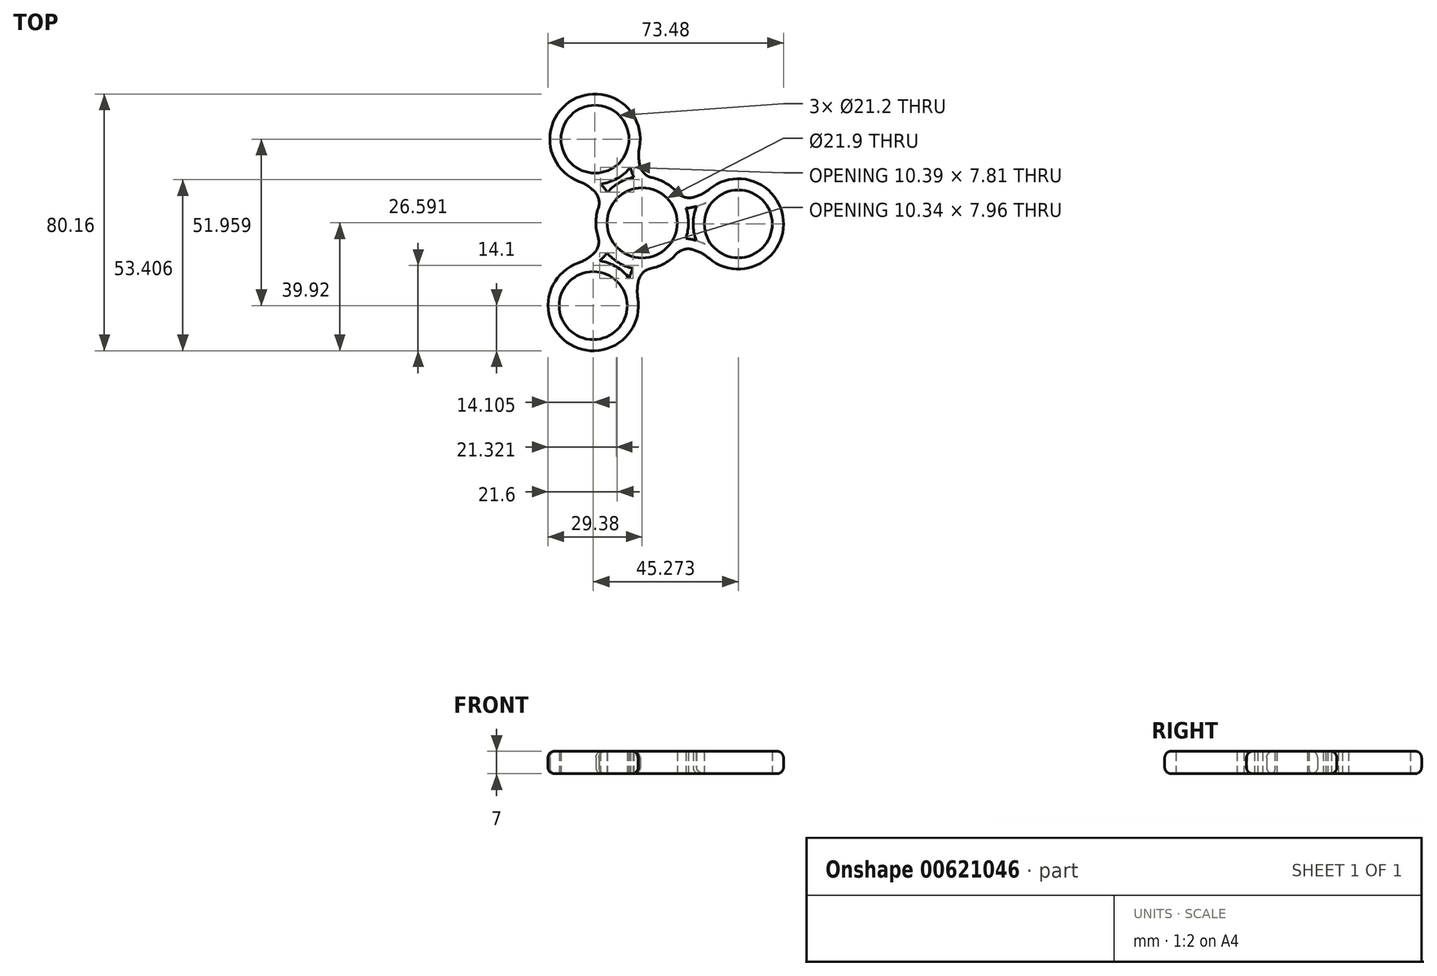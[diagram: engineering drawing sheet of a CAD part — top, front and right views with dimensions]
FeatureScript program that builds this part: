
annotation { "Feature Type Name" : "Feature", "Feature Type Description" : "" }
export const myFeature = defineFeature(function(context is Context, id is Id, definition is map)
    precondition{}
    {
        {
            var Q0;
            Q0=qCreatedBy(makeId("Top.planeOp"),FACE);
            var sketch = newSketch(context, id + "F0", { "sketchPlane" : qUnion([Q0])});
            skCircle(sketch, "E0", {"center": v(0, 0) * mm, "radius": 10.95 * mm});
            skCircle(sketch, "E1.0", {"center": v(0, 0) * mm, "radius": 14.45 * mm});
            skCircle(sketch, "E2.cCircle", {"center": v(0, 0) * mm, "radius": 15 * mm, "construction": true});
            skLineSegment(sketch, "E2.0", {"start": v(-14.72, 26.14) * mm, "end": v(30, -0.32) * mm, "construction": true});
            skLineSegment(sketch, "E2.1", {"start": v(30, -0.32) * mm, "end": v(-15.28, -25.82) * mm, "construction": true});
            skLineSegment(sketch, "E2.2", {"start": v(-15.28, -25.82) * mm, "end": v(-14.72, 26.14) * mm, "construction": true});
            skPoint(sketch, "E2.0.midPoint", {"position": v(7.64, 12.9) * mm});
            skCircle(sketch, "E3", {"center": v(-14.72, 26.14) * mm, "radius": 10.6 * mm});
            skCircle(sketch, "E4", {"center": v(30, -0.32) * mm, "radius": 10.6 * mm});
            skCircle(sketch, "E5", {"center": v(-15.28, -25.82) * mm, "radius": 10.6 * mm});
            skCircle(sketch, "E6.0", {"center": v(-14.72, 26.14) * mm, "radius": 14.1 * mm});
            skCircle(sketch, "E7.0", {"center": v(-15.28, -25.82) * mm, "radius": 14.1 * mm});
            skCircle(sketch, "E8.0", {"center": v(30, -0.32) * mm, "radius": 14.1 * mm});
            skArc(sketch, "E9", {"start": v(-0.86, 23.57) * mm, "mid": v(5.58, 9.42) * mm, "end": v(21.07, 10.6) * mm});
            skArc(sketch, "E10", {"start": v(20.84, -11.04) * mm, "mid": v(5.37, -9.54) * mm, "end": v(-1.36, -23.55) * mm});
            skArc(sketch, "E11", {"start": v(-19.99, -12.53) * mm, "mid": v(-10.95, 0.12) * mm, "end": v(-19.71, 12.95) * mm});
            skArc(sketch, "E12.0", {"start": v(-18.98, -15.36) * mm, "mid": v(-7.95, 0.08) * mm, "end": v(-18.65, 15.76) * mm});
            skArc(sketch, "E13.0", {"start": v(-3.8, 24.12) * mm, "mid": v(4.05, 6.84) * mm, "end": v(22.97, 8.27) * mm});
            skArc(sketch, "E14.0", {"start": v(22.8, -8.76) * mm, "mid": v(3.9, -6.93) * mm, "end": v(-4.32, -24.03) * mm});
            skSolve(sketch);
        }
        {
            var Q0;
            Q0=qSketchRegion(id+"F0",true);
            var Q1;
            {var subQ0=sQuery(id+"F0.wireOp",EDGE,"E13.0");var subQ1=sQuery(id+"F0.wireOp",EDGE,"E0");var subQ2=makeQuery(id+"F0.imprint","INTERSECT",VERTEX,{"disambiguationData":[OD(1.0)],"derivedFrom":[subQ1,subQ0]});Q1=makeQuery(id+"F0.imprint","IMPRINT",FACE,{"disambiguationData":[TD([[makeQuery(id+"F0.imprint","IMPRINT",EDGE,{"disambiguationData":[TD([[subQ2,-1.0]])],"derivedFrom":subQ1}),-1.0]])]});}
            var Q2;
            {var subQ0=sQuery(id+"F0.wireOp",EDGE,"E13.0");var subQ1=sQuery(id+"F0.wireOp",EDGE,"E0");var subQ2=makeQuery(id+"F0.imprint","INTERSECT",VERTEX,{"disambiguationData":[OD(0.0)],"derivedFrom":[subQ1,subQ0]});Q2=makeQuery(id+"F0.imprint","IMPRINT",FACE,{"disambiguationData":[TD([[makeQuery(id+"F0.imprint","IMPRINT",EDGE,{"disambiguationData":[TD([[subQ2,1.0]])],"derivedFrom":subQ1}),-1.0]])]});}
            var Q3;
            {var subQ0=sQuery(id+"F0.wireOp",EDGE,"E12.0");var subQ1=sQuery(id+"F0.wireOp",EDGE,"E0");var subQ2=makeQuery(id+"F0.imprint","INTERSECT",VERTEX,{"disambiguationData":[OD(1.0)],"derivedFrom":[subQ1,subQ0]});Q3=makeQuery(id+"F0.imprint","IMPRINT",FACE,{"disambiguationData":[TD([[makeQuery(id+"F0.imprint","IMPRINT",EDGE,{"disambiguationData":[TD([[subQ2,-1.0]])],"derivedFrom":subQ1}),-1.0]])]});}
            extrude(context, id + "F1", {"entities" : qUnion([Q0, Q1, Q2, Q3]), "depth" : 7 * mm, "offsetDistance" : 25 * mm});
        }
        {
            var Q0;
            {var subQ0=sQuery(id+"F0.wireOp",EDGE,"E10");var subQ1=sQuery(id+"F0.wireOp",EDGE,"E1.0");Q0=makeQuery(id+"F1.opExtrude","SWEPT_EDGE",EDGE,{"disambiguationData":[OSD([subQ1,subQ0]),TDD([makeQuery(id+"F0.imprint","INTERSECT",VERTEX,{"disambiguationData":[OD(0.0)],"derivedFrom":[subQ1,subQ0]})])]});}
            var Q1;
            {var subQ0=sQuery(id+"F0.wireOp",EDGE,"E10");var subQ1=sQuery(id+"F0.wireOp",EDGE,"E1.0");Q1=makeQuery(id+"F1.opExtrude","SWEPT_EDGE",EDGE,{"disambiguationData":[OSD([subQ1,subQ0]),TDD([makeQuery(id+"F0.imprint","INTERSECT",VERTEX,{"disambiguationData":[OD(1.0)],"derivedFrom":[subQ1,subQ0]})])]});}
            var Q2;
            {var subQ0=sQuery(id+"F0.wireOp",EDGE,"E9");var subQ1=sQuery(id+"F0.wireOp",EDGE,"E1.0");Q2=makeQuery(id+"F1.opExtrude","SWEPT_EDGE",EDGE,{"disambiguationData":[OSD([subQ1,subQ0]),TDD([makeQuery(id+"F0.imprint","INTERSECT",VERTEX,{"disambiguationData":[OD(1.0)],"derivedFrom":[subQ1,subQ0]})])]});}
            var Q3;
            {var subQ0=sQuery(id+"F0.wireOp",EDGE,"E9");var subQ1=sQuery(id+"F0.wireOp",EDGE,"E1.0");Q3=makeQuery(id+"F1.opExtrude","SWEPT_EDGE",EDGE,{"disambiguationData":[OSD([subQ1,subQ0]),TDD([makeQuery(id+"F0.imprint","INTERSECT",VERTEX,{"disambiguationData":[OD(0.0)],"derivedFrom":[subQ1,subQ0]})])]});}
            var Q4;
            {var subQ0=sQuery(id+"F0.wireOp",EDGE,"E11");var subQ1=sQuery(id+"F0.wireOp",EDGE,"E1.0");Q4=makeQuery(id+"F1.opExtrude","SWEPT_EDGE",EDGE,{"disambiguationData":[OSD([subQ1,subQ0]),TDD([makeQuery(id+"F0.imprint","INTERSECT",VERTEX,{"disambiguationData":[OD(1.0)],"derivedFrom":[subQ1,subQ0]})])]});}
            var Q5;
            {var subQ0=sQuery(id+"F0.wireOp",EDGE,"E11");var subQ1=sQuery(id+"F0.wireOp",EDGE,"E1.0");Q5=makeQuery(id+"F1.opExtrude","SWEPT_EDGE",EDGE,{"disambiguationData":[OSD([subQ1,subQ0]),TDD([makeQuery(id+"F0.imprint","INTERSECT",VERTEX,{"disambiguationData":[OD(0.0)],"derivedFrom":[subQ1,subQ0]})])]});}
            fillet(context, id + "F2", {"entities" : qUnion([Q0, Q1, Q2, Q3, Q4, Q5]), "radius" : 5 * mm, "tangentPropagation" : true, "allowEdgeOverflow" : false});
        }
        {
            var Q0;
            Q0=makeQuery(id+"F1.opExtrude","CAP_EDGE",EDGE,{"disambiguationData":[OSD([sQuery(id+"F0.wireOp",EDGE,"E8.0")])],"isStart":true});
            var Q1;
            {var subQ0=sQuery(id+"F0.wireOp",EDGE,"E10");var subQ1=sQuery(id+"F0.wireOp",EDGE,"E1.0");Q1=makeQuery(id+"F1.opExtrude","CAP_EDGE",EDGE,{"disambiguationData":[OSD([subQ1]),TDD([makeQuery(id+"F0.imprint","IMPRINT",EDGE,{"disambiguationData":[TD([[makeQuery(id+"F0.imprint","INTERSECT",VERTEX,{"disambiguationData":[OD(0.0)],"derivedFrom":[subQ1,subQ0]}),-1.0]])],"derivedFrom":subQ1})])],"isStart":false});}
            fillet(context, id + "F3", {"entities" : qUnion([Q0, Q1]), "radius" : 2 * mm, "tangentPropagation" : true, "allowEdgeOverflow" : false});
        }
    });
